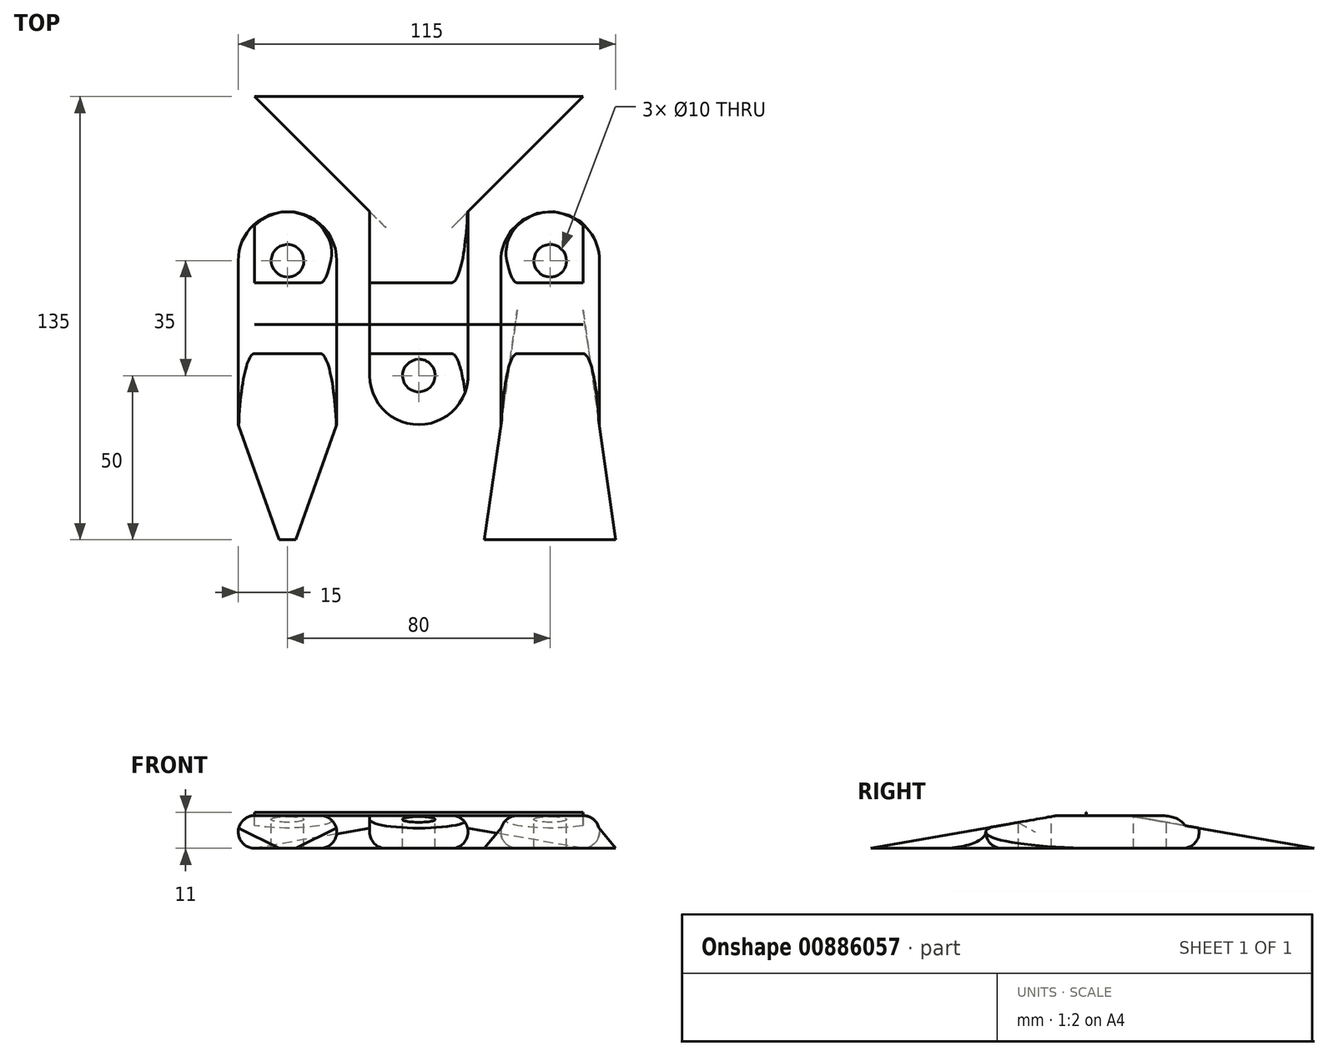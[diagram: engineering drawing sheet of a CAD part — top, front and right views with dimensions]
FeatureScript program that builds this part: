
annotation { "Feature Type Name" : "Feature", "Feature Type Description" : "" }
export const myFeature = defineFeature(function(context is Context, id is Id, definition is map)
    precondition{}
    {
        {
            var Q0;
            Q0=qCreatedBy(makeId("Top.planeOp"),FACE);
            var sketch = newSketch(context, id + "F0", { "sketchPlane" : qUnion([Q0])});
            skLineSegment(sketch, "E0", {"start": v(-50, 35) * mm, "end": v(50, 35) * mm});
            skLineSegment(sketch, "E1", {"start": v(50, 35) * mm, "end": v(15, 0) * mm});
            skLineSegment(sketch, "E2", {"start": v(15, 0) * mm, "end": v(15, -65) * mm});
            skLineSegment(sketch, "E3", {"start": v(15, -65) * mm, "end": v(-15, -65) * mm});
            skLineSegment(sketch, "E4", {"start": v(-15, -65) * mm, "end": v(-15, 0) * mm});
            skLineSegment(sketch, "E5", {"start": v(-15, 0) * mm, "end": v(-50, 35) * mm});
            skLineSegment(sketch, "E6", {"start": v(60, -100) * mm, "end": v(20, -100) * mm});
            skLineSegment(sketch, "E7", {"start": v(20, -100) * mm, "end": v(25, -65) * mm});
            skLineSegment(sketch, "E8", {"start": v(25, -65) * mm, "end": v(25, 0) * mm});
            skLineSegment(sketch, "E9", {"start": v(25, 0) * mm, "end": v(55, 0) * mm});
            skLineSegment(sketch, "E10", {"start": v(55, 0) * mm, "end": v(55, -65) * mm});
            skLineSegment(sketch, "E11", {"start": v(55, -65) * mm, "end": v(60, -100) * mm});
            skLineSegment(sketch, "E12", {"start": v(40, 0) * mm, "end": v(40, -100) * mm, "construction": true});
            skLineSegment(sketch, "E13", {"start": v(-37.5, -100) * mm, "end": v(-42.5, -100) * mm});
            skLineSegment(sketch, "E14", {"start": v(-42.5, -100) * mm, "end": v(-55, -65) * mm});
            skLineSegment(sketch, "E15", {"start": v(-55, -65) * mm, "end": v(-55, 0) * mm});
            skLineSegment(sketch, "E16", {"start": v(-55, 0) * mm, "end": v(-25, 0) * mm});
            skLineSegment(sketch, "E17", {"start": v(-25, 0) * mm, "end": v(-25, -65) * mm});
            skLineSegment(sketch, "E18", {"start": v(-25, -65) * mm, "end": v(-37.5, -100) * mm});
            skLineSegment(sketch, "E19", {"start": v(-40, 0) * mm, "end": v(-40, -100) * mm, "construction": true});
            skSolve(sketch);
        }
        {
            var Q0;
            Q0 = qSketchRegion(id + "F0", true);
            extrude(context, id + "F1", {"entities" : qUnion([Q0]), "depth" : 10 * mm, "offsetDistance" : 25 * mm, "symmetric" : true});
        }
        {
            var Q0;
            Q0=qCreatedBy(makeId("Right.planeOp"),FACE);
            var sketch = newSketch(context, id + "F2", { "sketchPlane" : qUnion([Q0])});
            skLineSegment(sketch, "E20", {"start": v(35, -5) * mm, "end": v(-21.71, 5) * mm});
            skLineSegment(sketch, "E21", {"start": v(-21.71, 5) * mm, "end": v(35, 5) * mm});
            skLineSegment(sketch, "E22", {"start": v(35, 5) * mm, "end": v(35, -5) * mm});
            skSolve(sketch);
        }
        {
            var Q0;
            Q0 = qSketchRegion(id + "F2", true);
            extrude(context, id + "F3", {"entities" : qUnion([Q0]), "operationType" : NewBodyOperationType.REMOVE, "oppositeDirection" : true, "depth" : 100 * mm, "offsetDistance" : 25 * mm, "symmetric" : true});
        }
        {
            var Q0;
            Q0=qCreatedBy(makeId("Right.planeOp"),FACE);
            cPlane(context, id + "F4", {"entities" : qUnion([Q0]), "cplaneType" : CPlaneType.OFFSET, "offset" : 45 * mm, "width" : 150 * mm, "height" : 150 * mm});
        }
        {
            var Q0;
            Q0=qCreatedBy(id+"F4.planeOp",FACE);
            var sketch = newSketch(context, id + "F5", { "sketchPlane" : qUnion([Q0])});
            skLineSegment(sketch, "E23", {"start": v(-100, -5) * mm, "end": v(-100, 5) * mm});
            skLineSegment(sketch, "E24", {"start": v(-100, 5) * mm, "end": v(-43.29, 5) * mm});
            skLineSegment(sketch, "E25", {"start": v(-43.29, 5) * mm, "end": v(-100, -5) * mm});
            skSolve(sketch);
        }
        {
            var Q0;
            Q0 = qSketchRegion(id + "F5", true);
            extrude(context, id + "F6", {"entities" : qUnion([Q0]), "operationType" : NewBodyOperationType.REMOVE, "depth" : 50 * mm, "offsetDistance" : 25 * mm, "hasSecondDirection" : true, "secondDirectionOppositeDirection" : true, "secondDirectionDepth" : 171 * mm});
        }
        {
            var Q0;
            Q0=makeQuery(id+"F1.opExtrude","SWEPT_EDGE",EDGE,{"disambiguationData":[OSD([sQuery(id+"F0.wireOp",EDGE,"E2"),sQuery(id+"F0.wireOp",EDGE,"E3")])]});
            var Q1;
            Q1=makeQuery(id+"F1.opExtrude","SWEPT_EDGE",EDGE,{"disambiguationData":[OSD([sQuery(id+"F0.wireOp",EDGE,"E3"),sQuery(id+"F0.wireOp",EDGE,"E4")])]});
            var Q2;
            Q2=makeQuery(id+"F1.opExtrude","SWEPT_EDGE",EDGE,{"disambiguationData":[OSD([sQuery(id+"F0.wireOp",EDGE,"E8"),sQuery(id+"F0.wireOp",EDGE,"E9")])]});
            var Q3;
            Q3=makeQuery(id+"F1.opExtrude","SWEPT_EDGE",EDGE,{"disambiguationData":[OSD([sQuery(id+"F0.wireOp",EDGE,"E9"),sQuery(id+"F0.wireOp",EDGE,"E10")])]});
            var Q4;
            Q4=makeQuery(id+"F1.opExtrude","SWEPT_EDGE",EDGE,{"disambiguationData":[OSD([sQuery(id+"F0.wireOp",EDGE,"E15"),sQuery(id+"F0.wireOp",EDGE,"E16")])]});
            var Q5;
            Q5=makeQuery(id+"F1.opExtrude","SWEPT_EDGE",EDGE,{"disambiguationData":[OSD([sQuery(id+"F0.wireOp",EDGE,"E16"),sQuery(id+"F0.wireOp",EDGE,"E17")])]});
            fillet(context, id + "F7", {"entities" : qUnion([Q0, Q1, Q2, Q3, Q4, Q5]), "radius" : 15 * mm, "tangentPropagation" : true, "allowEdgeOverflow" : false});
        }
        {
            var Q0;
            Q0=makeQuery(id+"F1.opExtrude","CAP_EDGE",EDGE,{"disambiguationData":[OSD([sQuery(id+"F0.wireOp",EDGE,"E2")])],"isStart":false});
            var Q1;
            Q1=makeQuery(id+"F1.opExtrude","CAP_EDGE",EDGE,{"disambiguationData":[OSD([sQuery(id+"F0.wireOp",EDGE,"E2")])],"isStart":true});
            var Q2;
            Q2=makeQuery(id+"F1.opExtrude","CAP_EDGE",EDGE,{"disambiguationData":[OSD([sQuery(id+"F0.wireOp",EDGE,"E10")])],"isStart":false});
            var Q3;
            Q3=makeQuery(id+"F1.opExtrude","CAP_EDGE",EDGE,{"disambiguationData":[OSD([sQuery(id+"F0.wireOp",EDGE,"E10")])],"isStart":true});
            var Q4;
            Q4=makeQuery(id+"F1.opExtrude","CAP_EDGE",EDGE,{"disambiguationData":[OSD([sQuery(id+"F0.wireOp",EDGE,"E15")])],"isStart":true});
            var Q5;
            Q5=makeQuery(id+"F1.opExtrude","CAP_EDGE",EDGE,{"disambiguationData":[OSD([sQuery(id+"F0.wireOp",EDGE,"E15")])],"isStart":false});
            fillet(context, id + "F8", {"entities" : qUnion([Q0, Q1, Q2, Q3, Q4, Q5]), "radius" : 5 * mm, "tangentPropagation" : true, "allowEdgeOverflow" : false});
        }
        {
            var Q0;
            Q0=makeQuery(id+"F1.opExtrude","CAP_FACE",FACE,{"disambiguationData":[OSD([sQuery(id+"F0.wireOp",EDGE,"E6"),sQuery(id+"F0.wireOp",EDGE,"E7"),sQuery(id+"F0.wireOp",EDGE,"E8"),sQuery(id+"F0.wireOp",EDGE,"E9"),sQuery(id+"F0.wireOp",EDGE,"E10"),sQuery(id+"F0.wireOp",EDGE,"E11")])],"isStart":false});
            var sketch = newSketch(context, id + "F9", { "sketchPlane" : qUnion([Q0])});
            skCircle(sketch, "E26", {"center": v(-40, -15) * mm, "radius": 5 * mm});
            skCircle(sketch, "E27", {"center": v(40, -15) * mm, "radius": 5 * mm});
            skCircle(sketch, "E28", {"center": v(0, -50) * mm, "radius": 5 * mm});
            skArc(sketch, "E29.0", {"start": v(-30, -15) * mm, "mid": v(-40, -5) * mm, "end": v(-50, -15) * mm, "construction": true});
            skArc(sketch, "E30.0", {"start": v(-10, -50) * mm, "mid": v(0, -60) * mm, "end": v(10, -50) * mm, "construction": true});
            skArc(sketch, "E31.0", {"start": v(50, -15) * mm, "mid": v(40, -5) * mm, "end": v(30, -15) * mm, "construction": true});
            skSolve(sketch);
        }
        {
            var Q0;
            Q0 = qSketchRegion(id + "F9", true);
            extrude(context, id + "F10", {"entities" : qUnion([Q0]), "operationType" : NewBodyOperationType.REMOVE, "oppositeDirection" : true, "depth" : 25 * mm, "offsetDistance" : 25 * mm});
        }
        {
            var Q0;
            Q0=makeQuery(id+"F1.opExtrude","CAP_FACE",FACE,{"disambiguationData":[OSD([sQuery(id+"F0.wireOp",EDGE,"E13"),sQuery(id+"F0.wireOp",EDGE,"E14"),sQuery(id+"F0.wireOp",EDGE,"E15"),sQuery(id+"F0.wireOp",EDGE,"E16"),sQuery(id+"F0.wireOp",EDGE,"E17"),sQuery(id+"F0.wireOp",EDGE,"E18")])],"isStart":false});
            var sketch = newSketch(context, id + "F11", { "sketchPlane" : qUnion([Q0])});
            skLineSegment(sketch, "E32.bottom", {"start": v(-50, -34.38) * mm, "end": v(50, -34.38) * mm});
            skLineSegment(sketch, "E32.top", {"start": v(-50, -34.43) * mm, "end": v(50, -34.43) * mm});
            skLineSegment(sketch, "E32.left", {"start": v(-50, -34.38) * mm, "end": v(-50, -34.43) * mm});
            skLineSegment(sketch, "E32.right", {"start": v(50, -34.38) * mm, "end": v(50, -34.43) * mm});
            skSolve(sketch);
        }
        {
            var Q0;
            Q0 = qSketchRegion(id + "F11", true);
            extrude(context, id + "F12", {"entities" : qUnion([Q0]), "operationType" : NewBodyOperationType.ADD, "depth" : 1 * mm, "offsetDistance" : 25 * mm});
        }
    });
